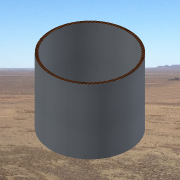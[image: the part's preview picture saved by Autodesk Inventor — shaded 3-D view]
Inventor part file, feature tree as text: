
AUTODESK INVENTOR PART (.ipt)
format: ipt  version: 2013 SP2 (Build 170200200, 200)  size: 133,632 bytes
history: native  units: in
note: dims shown in document units (in); Inventor stores cm internally (conversion verified against a paired STEP export)
features: extrude x1, sketch x1
ambient origin geometry x8: Origin, YZ Plane, XZ Plane, XY Plane, X Axis, Y Axis, Z Axis, Center Point
bodies: Solid1 (feature_tree)
feature tree (2):
  extrude  "Extrusion1"  Depth=0.375in
  sketch  "Sketch1"  dims[d0=12.0in d2=0.375in d3=10.0in d4=0.0in]
